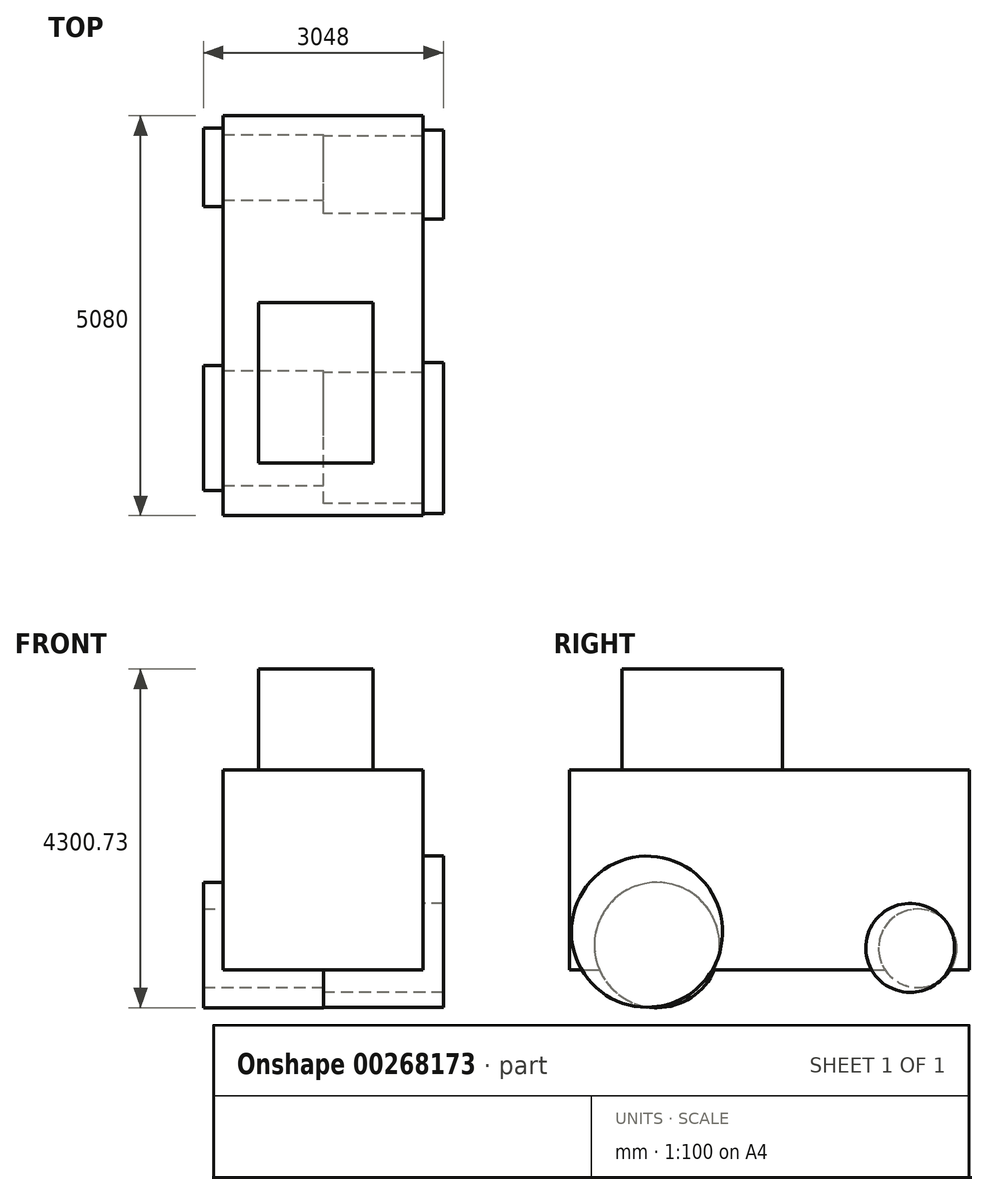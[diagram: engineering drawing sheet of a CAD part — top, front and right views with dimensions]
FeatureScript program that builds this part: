
annotation { "Feature Type Name" : "Feature", "Feature Type Description" : "" }
export const myFeature = defineFeature(function(context is Context, id is Id, definition is map)
    precondition{}
    {
        {
            var Q0;
            Q0=qCreatedBy(makeId("Front.planeOp"),FACE);
            var sketch = newSketch(context, id + "F0", { "sketchPlane" : qUnion([Q0])});
            skLineSegment(sketch, "E0.bottom", {"start": v(-1275.38, 1261.74) * mm, "end": v(1264.62, 1261.74) * mm});
            skLineSegment(sketch, "E0.top", {"start": v(-1275.38, -1278.26) * mm, "end": v(1264.62, -1278.26) * mm});
            skLineSegment(sketch, "E0.left", {"start": v(-1275.38, 1261.74) * mm, "end": v(-1275.38, -1278.26) * mm});
            skLineSegment(sketch, "E0.right", {"start": v(1264.62, 1261.74) * mm, "end": v(1264.62, -1278.26) * mm});
            skSolve(sketch);
        }
        {
            var Q0;
            Q0 = qSketchRegion(id + "F0", true);
            extrude(context, id + "F1", {"entities" : qUnion([Q0]), "depth" : 5080 * mm});
        }
        {
            var Q0;
            Q0=qCreatedBy(makeId("Top.planeOp"),FACE);
            var sketch = newSketch(context, id + "F2", { "sketchPlane" : qUnion([Q0])});
            skLineSegment(sketch, "E1.bottom", {"start": v(-823.2, -4412.23) * mm, "end": v(627.27, -4412.23) * mm});
            skLineSegment(sketch, "E1.top", {"start": v(-823.2, -2375.4) * mm, "end": v(627.27, -2375.4) * mm});
            skLineSegment(sketch, "E1.left", {"start": v(-823.2, -4412.23) * mm, "end": v(-823.2, -2375.4) * mm});
            skLineSegment(sketch, "E1.right", {"start": v(627.27, -4412.23) * mm, "end": v(627.27, -2375.4) * mm});
            skSolve(sketch);
        }
        {
            var Q0;
            Q0 = qSketchRegion(id + "F2", true);
            extrude(context, id + "F3", {"entities" : qUnion([Q0]), "operationType" : NewBodyOperationType.ADD, "depth" : 2540 * mm});
        }
        {
            var Q0;
            Q0=qCreatedBy(makeId("Right.planeOp"),FACE);
            var sketch = newSketch(context, id + "F4", { "sketchPlane" : qUnion([Q0])});
            skCircle(sketch, "E2", {"center": v(-750.07, -1000.96) * mm, "radius": 564.94 * mm});
            skCircle(sketch, "E3", {"center": v(-4093.33, -795.22) * mm, "radius": 960.28 * mm});
            skSolve(sketch);
        }
        {
            var Q0;
            Q0 = qSketchRegion(id + "F4", true);
            extrude(context, id + "F5", {"entities" : qUnion([Q0]), "operationType" : NewBodyOperationType.ADD, "depth" : 1524 * mm});
        }
        {
            var Q0;
            Q0=qCreatedBy(makeId("Right.planeOp"),FACE);
            var sketch = newSketch(context, id + "F6", { "sketchPlane" : qUnion([Q0])});
            skCircle(sketch, "E4", {"center": v(-653.75, -1006.32) * mm, "radius": 497.62 * mm});
            skCircle(sketch, "E5", {"center": v(-3966.4, -965.17) * mm, "radius": 795.56 * mm});
            skSolve(sketch);
        }
        {
            var Q0;
            Q0 = qSketchRegion(id + "F6", true);
            extrude(context, id + "F7", {"entities" : qUnion([Q0]), "operationType" : NewBodyOperationType.ADD, "oppositeDirection" : true, "depth" : 1524 * mm});
        }
    });
